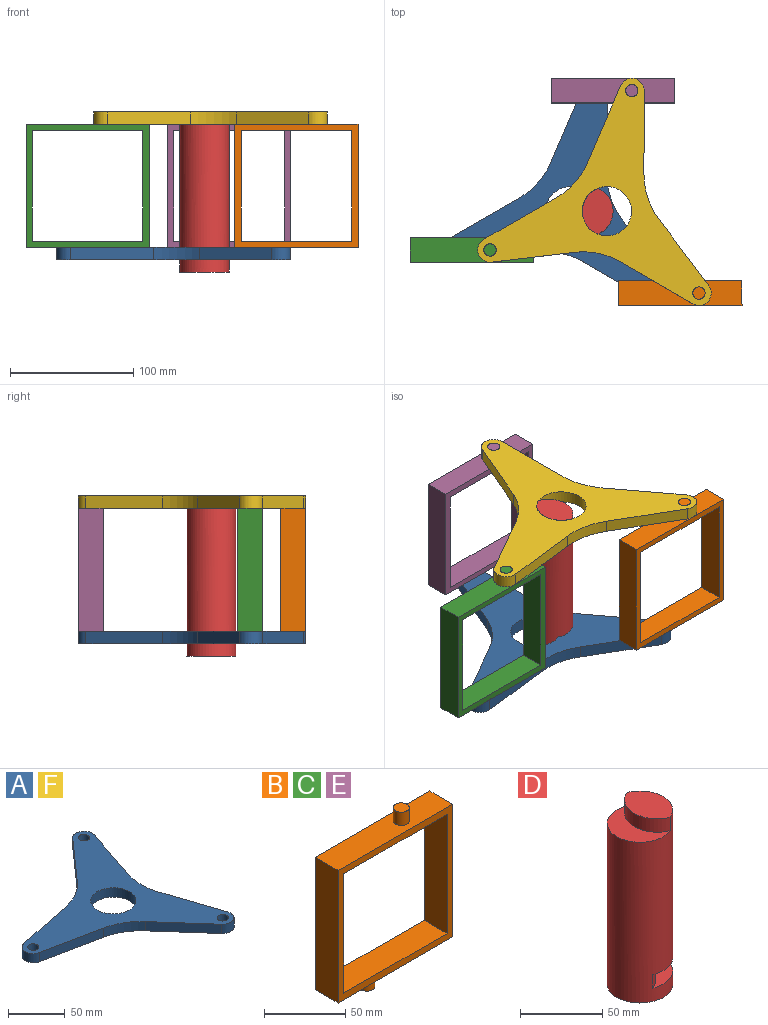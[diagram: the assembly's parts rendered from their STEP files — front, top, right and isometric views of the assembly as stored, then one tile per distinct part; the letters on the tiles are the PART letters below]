
ASSEMBLY  parts=6 mates=8
PART A: 18 faces, bbox 170x193.2x10 mm
  f0: plane 66.56x13.59mm, normal (-0.2,0.98,0), area 679.3mm2, adj f1,f13,f14,f15
  f1: cylinder r=10mm len=19.6mm, axis (0,0,-1), area 273.9mm2, adj f0,f2,f13,f14
  f2: plane 66.56x13.59mm, normal (-0.2,-0.98,0), area 679.3mm2, adj f1,f13,f14,f16
  f3: plane 50.85x45.05mm, normal (-0.75,-0.66,0), area 679.3mm2, adj f4,f13,f14,f16
  f4: cylinder r=10mm len=17.49mm, axis (0,0,-1), area 273.9mm2, adj f3,f5,f13,f14
  f5: plane 64.43x21.51mm, normal (0.95,0.32,0), area 679.3mm2, adj f4,f13,f14,f17
  f6: plane 64.43x21.51mm, normal (0.95,-0.32,0), area 679.3mm2, adj f7,f13,f14,f17
  f7: cylinder r=10mm len=17.49mm, axis (0,0,-1), area 273.9mm2, adj f6,f10,f13,f14
  f8: cylinder r=20mm len=40mm, axis (0,0,-1), area 1256.6mm2, adj f13,f14
  f9: cylinder r=5mm len=10mm, axis (0,0,-1), area 314.2mm2, adj f13,f14
  f10: plane 50.85x45.05mm, normal (-0.75,0.66,0), area 679.3mm2, adj f7,f13,f14,f15
  f11: cylinder r=5mm len=10mm, axis (0,0,-1), area 314.2mm2, adj f13,f14
  f12: cylinder r=5mm len=10mm, axis (0,0,-1), area 314.2mm2, adj f13,f14
  f13: plane 193.21x170mm, normal (0,0,1), area 9900.3mm2, adj f0,f1,f2,f3,f4,f5,f6,f7
  f14: plane 193.21x170mm, normal (0,0,-1), area 9900.3mm2, adj f0,f1,f2,f3,f4,f5,f6,f7
  f15: cylinder r=60mm len=32.91mm, axis (0,0,1), area 386.7mm2, adj f0,f10,f13,f14
  f16: cylinder r=60mm len=32.91mm, axis (0,0,1), area 386.7mm2, adj f2,f3,f13,f14
  f17: cylinder r=60mm len=38mm, axis (0,0,-1), area 386.7mm2, adj f5,f6,f13,f14
PART B: 14 faces, bbox 100x20x120 mm
  f0: plane 100x20mm, normal (0,0,1), area 1921.5mm2, adj f1,f7,f8,f9,f10
  f1: plane 100x20mm, normal (-1,0,0), area 2000mm2, adj f0,f2,f8,f9
  f2: plane 100x20mm, normal (0,0,-1), area 1921.5mm2, adj f1,f7,f8,f9,f12
  f3: plane 90x20mm, normal (1,0,0), area 1800mm2, adj f4,f6,f8,f9
  f4: plane 90x20mm, normal (0,0,-1), area 1800mm2, adj f3,f5,f8,f9
  f5: plane 90x20mm, normal (-1,0,0), area 1800mm2, adj f4,f6,f8,f9
  f6: plane 90x20mm, normal (0,0,1), area 1800mm2, adj f3,f5,f8,f9
  f7: plane 100x20mm, normal (1,0,0), area 2000mm2, adj f0,f2,f8,f9
  f8: plane 100x100mm, normal (0,-1,0), area 1900mm2, adj f0,f1,f2,f3,f4,f5,f6,f7
  f9: plane 100x100mm, normal (0,1,0), area 1900mm2, adj f0,f1,f2,f3,f4,f5,f6,f7
  f10: cylinder r=5mm len=10mm, axis (0,0,-1), area 314.2mm2, adj f0,f11
  f11: plane 10x10mm, normal (0,0,1), area 78.5mm2, adj f10
  f12: cylinder r=5mm len=10mm, axis (0,0,1), area 314.2mm2, adj f2,f13
  f13: plane 10x10mm, normal (0,0,-1), area 78.5mm2, adj f12
PART C: same geometry as B
PART D: 8 faces, bbox 40x40x130 mm
  f0: cylinder r=20mm len=130mm, axis (0,0,-1), area 14772.1mm2, adj f1,f2,f3,f4,f5,f6,f7
  f1: plane 40x27.5mm, normal (0,0,1), area 585.6mm2, adj f0,f3
  f2: plane 40x27.5mm, normal (0,0,-1), area 585.6mm2, adj f0,f5
  f3: cylinder r=20mm len=37.08mm, axis (0,0,-1), area 474.6mm2, adj f0,f1,f4
  f4: plane 37.08x25mm, normal (0,0,1), area 671mm2, adj f0,f3
  f5: cylinder r=20mm len=37.08mm, axis (0,0,1), area 474.6mm2, adj f0,f2,f7
  f6: plane 40x40mm, normal (0,0,-1), area 1256.6mm2, adj f0
  f7: plane 40x27.5mm, normal (0,0,1), area 585.6mm2, adj f0,f5
PART E: same geometry as B
PART F: same geometry as A
PLACE A rot(axis=(0,0,1),18.3deg) t=(-15,0,-10)mm
PLACE B t=(74.7,-66.48,50)mm
PLACE C t=(-94.93,-31.45,50)mm
PLACE D at identity fixed
PLACE E t=(20.23,97.93,50)mm
PLACE F rot(axis=(0,0,1),18.3deg) t=(15,0,100)mm
MATE revolute B.f10 <-> F.f4  axis (0,0,1) through (89.7,-66.48,110)mm
MATE revolute B.f12 <-> A.f4  axis (0,0,-1) through (59.7,-66.48,-10)mm
MATE revolute E.f10 <-> F.f7  axis (0,0,1) through (35.23,97.93,110)mm
MATE revolute A.f8 <-> D.f5  axis (0,0,-1) through (-15,0,-10)mm
MATE parallel E.f7 <-> B.f7  axis (1,0,0) through (70.23,97.93,50)mm
MATE revolute C.f10 <-> F.f11  axis (0,0,1) through (-79.93,-31.45,110)mm
MATE revolute F.f8 <-> D.f3  axis (0,0,1) through (15,0,110)mm
MATE revolute C.f12 <-> A.f1  axis (0,0,-1) through (-109.93,-31.45,-10)mm
